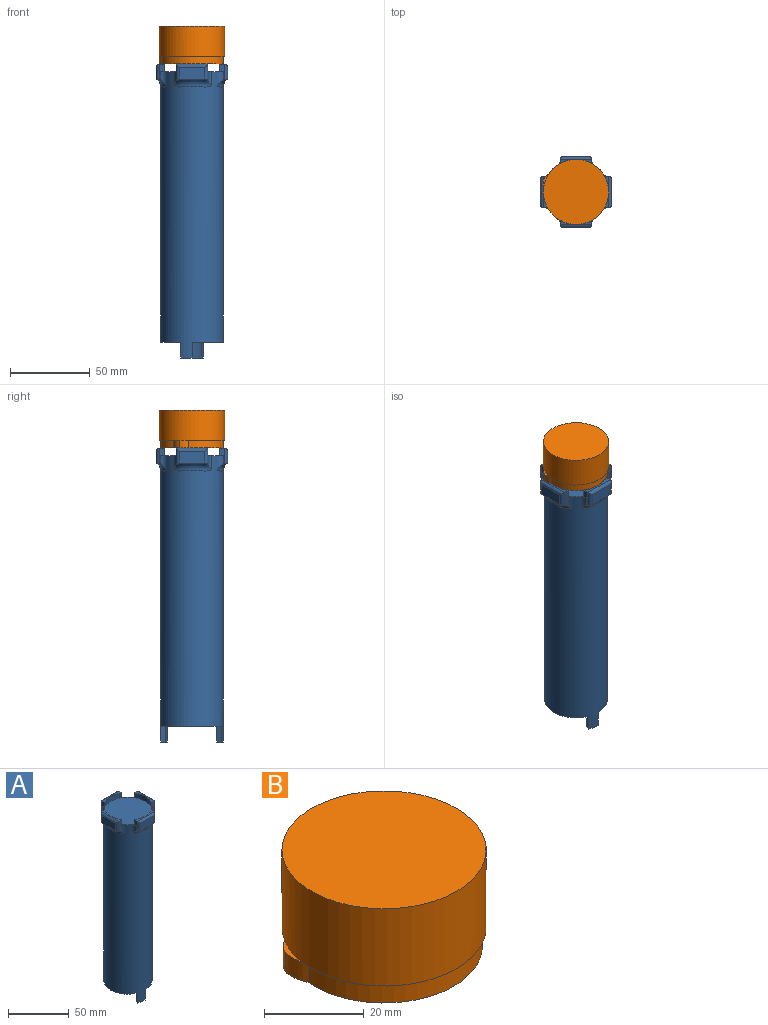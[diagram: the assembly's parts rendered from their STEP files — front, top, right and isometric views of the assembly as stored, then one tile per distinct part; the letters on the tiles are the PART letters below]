
ASSEMBLY  parts=2 mates=1
PART A: 56 faces, bbox 45.1x45.1x184.8 mm
  f0: plane 38.13x19.75mm, normal (0,0,-1), area 151.5mm2, adj f1,f48,f50,f53
  f1: cylinder r=19.75mm len=180mm, axis (0,0,1), area 20332.8mm2, adj f0,f2,f3,f24,f25,f26,f27,f28
  f2: plane 38.13x19.75mm, normal (0,0,-1), area 151.5mm2, adj f1,f48,f49,f52
  f3: plane 39.5x39.5mm, normal (0,0,1), area 1233.5mm2, adj f1,f4,f5,f7,f9,f10,f11,f14
  f4: cylinder r=19.75mm len=20mm, axis (0,0,-1), area 98.6mm2, adj f3,f5,f7,f8
  f5: plane 10.17x3.46mm, normal (1,0,0), area 20.3mm2, adj f3,f4,f8,f27,f34,f45
  f6: plane 16.12x7.52mm, normal (0,1,0), area 118.4mm2, adj f27,f45,f46,f47
  f7: plane 10.17x3.46mm, normal (-1,0,0), area 20.3mm2, adj f3,f4,f8,f27,f35,f47
  f8: plane 20x3.44mm, normal (0,0,1), area 32mm2, adj f4,f5,f7,f46
  f9: cylinder r=19.75mm len=20mm, axis (0,0,-1), area 98.6mm2, adj f3,f10,f11,f13
  f10: plane 10.17x3.46mm, normal (0,1,0), area 20.3mm2, adj f3,f9,f13,f25,f32,f41
  f11: plane 10.17x3.46mm, normal (0,-1,0), area 20.3mm2, adj f3,f9,f13,f25,f33,f39
  f12: plane 16.12x7.52mm, normal (1,0,0), area 118.4mm2, adj f25,f39,f40,f41
  f13: plane 20x3.44mm, normal (0,0,1), area 32mm2, adj f9,f10,f11,f40
  f14: cylinder r=19.75mm len=20mm, axis (0,0,-1), area 98.6mm2, adj f3,f15,f16,f18
  f15: plane 10.17x3.46mm, normal (1,0,0), area 20.3mm2, adj f3,f14,f18,f24,f30,f38
  f16: plane 10.17x3.46mm, normal (-1,0,0), area 20.3mm2, adj f3,f14,f18,f24,f31,f36
  f17: plane 16.12x7.52mm, normal (0,-1,0), area 118.4mm2, adj f24,f36,f37,f38
  f18: plane 20x3.44mm, normal (0,0,1), area 32mm2, adj f14,f15,f16,f37
  f19: cylinder r=19.75mm len=20mm, axis (0,0,-1), area 98.6mm2, adj f3,f20,f22,f23
  f20: plane 10.17x3.46mm, normal (0,1,0), area 20.3mm2, adj f3,f19,f23,f26,f28,f44
  f21: plane 16.12x7.52mm, normal (-1,0,0), area 118.4mm2, adj f26,f42,f43,f44
  f22: plane 10.17x3.46mm, normal (0,-1,0), area 20.3mm2, adj f3,f19,f23,f26,f29,f42
  f23: plane 20x3.44mm, normal (0,0,1), area 32mm2, adj f19,f20,f22,f43
  f24: bspline ~30.63x8.64mm, area 138.5mm2, adj f1,f15,f16,f17,f30,f31,f36,f38
  f25: bspline ~30.63x8.64mm, area 138.5mm2, adj f1,f10,f11,f12,f32,f33,f39,f41
  f26: bspline ~30.63x8.64mm, area 138.5mm2, adj f1,f20,f21,f22,f28,f29,f42,f44
  f27: bspline ~30.63x8.64mm, area 138.5mm2, adj f1,f5,f6,f7,f34,f35,f45,f47
  f28: cylinder r=5mm len=8.85mm, axis (0,0,1), area 32.9mm2, adj f1,f3,f20,f26
  f29: cylinder r=5mm len=8.85mm, axis (0,0,1), area 32.9mm2, adj f1,f3,f22,f26
  f30: cylinder r=5mm len=8.85mm, axis (0,0,1), area 32.9mm2, adj f1,f3,f15,f24
  f31: cylinder r=5mm len=8.85mm, axis (0,0,1), area 32.9mm2, adj f1,f3,f16,f24
  f32: cylinder r=5mm len=8.85mm, axis (0,0,1), area 32.9mm2, adj f1,f3,f10,f25
  f33: cylinder r=5mm len=8.85mm, axis (0,0,1), area 32.9mm2, adj f1,f3,f11,f25
  f34: cylinder r=5mm len=8.85mm, axis (0,0,1), area 32.9mm2, adj f1,f3,f5,f27
  f35: cylinder r=5mm len=8.85mm, axis (0,0,1), area 32.9mm2, adj f1,f3,f7,f27
  f36: cylinder r=2mm len=9.8mm, axis (0,0,1), area 27mm2, adj f16,f17,f24,f37
  f37: cylinder r=2mm len=20mm, axis (-1,0,0), area 56.5mm2, adj f17,f18,f36,f38
  f38: cylinder r=2mm len=9.8mm, axis (0,0,-1), area 27mm2, adj f15,f17,f24,f37
  f39: cylinder r=2mm len=9.8mm, axis (0,0,1), area 27mm2, adj f11,f12,f25,f40
  f40: cylinder r=2mm len=20mm, axis (0,-1,0), area 56.5mm2, adj f12,f13,f39,f41
  f41: cylinder r=2mm len=9.8mm, axis (0,0,-1), area 27mm2, adj f10,f12,f25,f40
  f42: cylinder r=2mm len=9.8mm, axis (0,0,1), area 27mm2, adj f21,f22,f26,f43
  f43: cylinder r=2mm len=20mm, axis (0,1,0), area 56.5mm2, adj f21,f23,f42,f44
  f44: cylinder r=2mm len=9.8mm, axis (0,0,-1), area 27mm2, adj f20,f21,f26,f43
  f45: cylinder r=2mm len=9.8mm, axis (0,0,-1), area 27mm2, adj f5,f6,f27,f46
  f46: cylinder r=2mm len=20mm, axis (1,0,0), area 56.5mm2, adj f6,f8,f45,f47
  f47: cylinder r=2mm len=9.8mm, axis (0,0,1), area 27mm2, adj f6,f7,f27,f46
  f48: cylinder r=16.75mm len=170mm, axis (0,0,1), area 16964.4mm2, adj f0,f2,f49,f50,f51,f52,f53,f54
  f49: plane 10x3mm, normal (1,0,0), area 30mm2, adj f1,f2,f48,f51
  f50: plane 10x2.79mm, normal (-0.93,0.37,0), area 30mm2, adj f0,f1,f48,f51
  f51: plane 7.23x4.16mm, normal (0,0,-1), area 20.5mm2, adj f1,f48,f49,f50
  f52: plane 10x2.79mm, normal (0.93,-0.37,0), area 30mm2, adj f1,f2,f48,f54
  f53: plane 10x3mm, normal (-1,0,0), area 30mm2, adj f0,f1,f48,f54
  f54: plane 7.23x4.16mm, normal (0,0,-1), area 20.5mm2, adj f1,f48,f52,f53
  f55: plane 33.5x33.5mm, normal (0,0,-1), area 881.4mm2, adj f48
PART B: 8 faces, bbox 41.1x41x23.7 mm
  f0: cylinder r=19.75mm len=39.5mm, axis (0,0,-1), area 535.4mm2, adj f1,f2,f4,f5
  f1: cylinder r=6.66mm len=4.7mm, axis (0,0,-1), area 26.8mm2, adj f0,f2,f3,f4,f5
  f2: cylinder r=8.21mm len=5.82mm, axis (0,0,-1), area 28.2mm2, adj f0,f1,f3,f4,f5
  f3: plane 7.53x3.19mm, normal (0,0,1), area 6.4mm2, adj f1,f2,f6
  f4: plane 40.33x39.5mm, normal (0,0,-1), area 1238.7mm2, adj f0,f1,f2
  f5: plane 41x41mm, normal (0,0,-1), area 87.9mm2, adj f0,f1,f2,f6
  f6: cylinder r=20.5mm len=41mm, axis (0,0,-1), area 2447.3mm2, adj f3,f5,f7
  f7: plane 41x41mm, normal (0,0,1), area 1320.3mm2, adj f6
PLACE A t=(-46.26,-26.41,-11.37)mm
PLACE B t=(-46.26,-26.41,78.63)mm
MATE slider B.f0 <-> A.f1  axis (0,0,-1) through (-46.26,-26.41,78.63)mm
